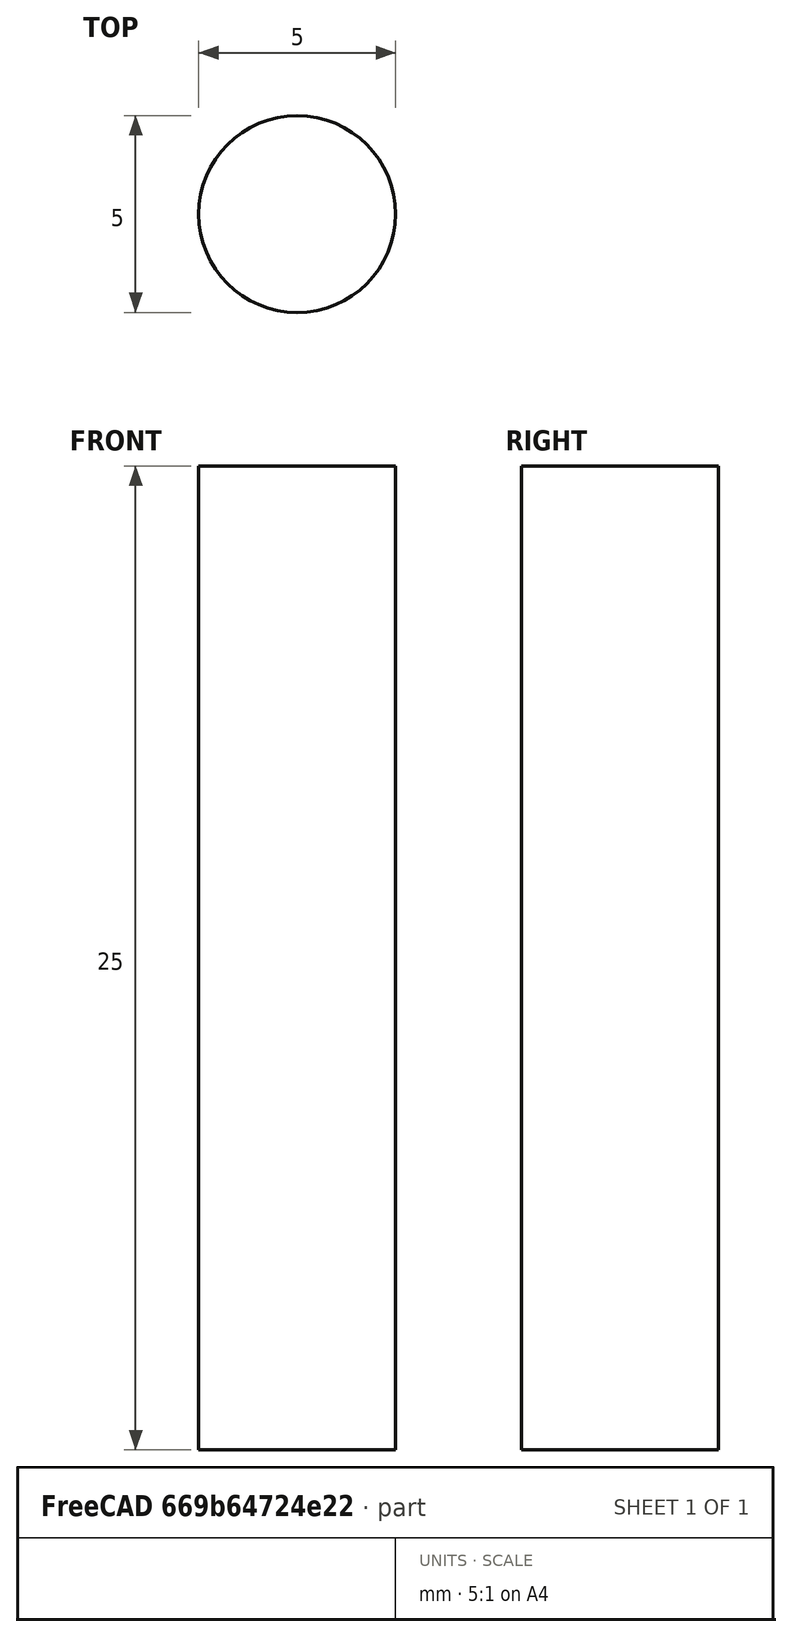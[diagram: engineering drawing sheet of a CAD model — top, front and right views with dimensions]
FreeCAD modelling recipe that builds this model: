
FCSTD DOCUMENT  (FreeCAD 1.0R39319 (Git))
Label: Airpods_2
License: All rights reserved
LicenseURL: https://en.wikipedia.org/wiki/All_rights_reserved
objects: Sketcher::SketchObject×6, Part::FeaturePython×5, Part::Part2DObjectPython×2, Part::Loft×2, Part::Extrusion×2, Part::MultiFuse×2, Part::RuledSurface×2, Part::Revolution×1, PartDesign::SubShapeBinder×1, App::DocumentObjectGroup×1
note: 29 computed .brp shape members not serialized (recipe doc carries the construction recipe); baked Part::Feature solids carry a one-line shape summary decoded from their .brp

FEATURE [Sketcher::SketchObject] Sketch  label="Front_profile"
  ArcFitTolerance = 1e-06
  FullyConstrained = true
  MakeInternals = false
  Placement = pos=(0,0,0) rot=(1,0,0;1.5708rad)
  sketch-geometry (18):
    g0-g4: Circle [constr] x5 (B-spline internal-alignment scaffolding for g5; pole/knot coordinates omitted)
    g5: BSplineCurve PolesCount=5 KnotsCount=3 Degree=3 IsPeriodic=0
    g6: GeomPoint [constr] X=-2 Y=0 Z=0
    g7: GeomPoint [constr] X=0 Y=3.5 Z=0
    g8: GeomPoint [constr] X=2 Y=0 Z=0
    g9: BSplineCurve PolesCount=5 KnotsCount=3 Degree=3 IsPeriodic=0
    g10-g14: Circle [constr] x5 (B-spline internal-alignment scaffolding for g9; pole/knot coordinates omitted)
    g15: GeomPoint [constr] X=-2 Y=0 Z=0
    g16: GeomPoint [constr] X=0 Y=-3.5 Z=0
    g17: GeomPoint [constr] X=2 Y=0 Z=0
  constraints (21):
    c: Weight(g0) = 1
    c: Equal(g0, g1-g4) x4
    c: InternalAlignment(g0-g4 -> g5) x5
    c: InternalAlignment(g6,g5)
    c: InternalAlignment(g7,g5)
    c: InternalAlignment(g8,g5)
    c: Distance(g0,g1) = 3.5
    c: PointOnObject(g0,g-1)
    c: PointOnObject(g2,g-2)
    c: PointOnObject(g4,g-1)
    c: Horizontal(g1,g3)
    c: Coincident(g7,g2)
    c: Vertical(g3,g5)
    c: Vertical(g1,g5)
    c: DistanceX(g5,g5) = 4
    c: Weight(g10) = 1
    c: Equal(g10, g11-g14) x4
    c: InternalAlignment(g10-g17 -> g9) x8
    c: Distance(g10,g11) = 3.5
    c: Coincident(g16,g12)
    c: Block(g9)
FEATURE [Sketcher::SketchObject] Sketch001  label="mid_profile"
  ArcFitTolerance = 1e-06
  FullyConstrained = true
  MakeInternals = false
  Placement = pos=(0,8,0) rot=(1,0,0;1.5708rad)
  sketch-geometry (5):
    g0: Ellipse CenterX=0 CenterY=0 CenterZ=0 NormalX=0 NormalY=0 NormalZ=1 MajorRadius=10 MinorRadius=6 AngleXU=-1.5708
    g1: LineSegment [constr] StartX=-3.26795e-06 StartY=-10 StartZ=0 EndX=3.26795e-06 EndY=10 EndZ=0
    g2: LineSegment [constr] StartX=6 StartY=-1.96077e-06 StartZ=0 EndX=-6 EndY=1.96077e-06 EndZ=0
    g3: GeomPoint [constr] X=-2.61436e-06 Y=-8 Z=0
    g4: GeomPoint [constr] X=2.61436e-06 Y=8 Z=0
  constraints (5):
    c: InternalAlignment(g1-g4 -> g0) x4
    c: Distance(g0,g1) = 10
    c: Angle(g1) = 1.5708
    c: Distance(g0,g2) = 6
    c: Coincident(g0,g-1)
FEATURE [Part::Part2DObjectPython] Clone2D  label="End_profile"  # Draft 2D object (typed FeaturePython)
  Fuse = false
  Objects = -> [Sketch001]
  Placement = pos=(0,10,0) rot=(1,0,0;1.5708rad)
  Scale = (1,1,1)
FEATURE [Part::Loft] Loft
  Closed = false
  MaxDegree = 5
  Ruled = false
  Sections = -> [Sketch,Sketch001,Clone2D]
  Solid = false
FEATURE [Sketcher::SketchObject] Sketch002  label="end_profilehalf"
  ArcFitTolerance = 1e-06
  ExternalGeometry = -> [Loft]
  FullyConstrained = true
  MakeInternals = false
  Placement = pos=(0,10,0) rot=(1,0,0;1.5708rad)
  sketch-geometry (5):
    g0: ArcOfEllipse CenterX=0 CenterY=0 CenterZ=0 NormalX=0 NormalY=0 NormalZ=1 MajorRadius=10 MinorRadius=6 AngleXU=-1.5708 StartAngle=1.5708 EndAngle=4.71239
    g1: LineSegment [constr] StartX=0 StartY=-10 StartZ=0 EndX=0 EndY=10 EndZ=0
    g2: LineSegment [constr] StartX=6 StartY=-1e-16 StartZ=0 EndX=-6 EndY=1e-16 EndZ=0
    g3: GeomPoint [constr] X=0 Y=-8 Z=0
    g4: GeomPoint [constr] X=0 Y=8 Z=0
  constraints (6):
    c: InternalAlignment(g1-g4 -> g0) x4
    c: Coincident(g0,g-1)
    c: Coincident(g0,g-3)
    c: PointOnObject(g0,g2)
    c: DistanceY(g-1,g1) = 10
    c: Vertical(g1)
FEATURE [Sketcher::SketchObject] Sketch003  label="Rev_axis_endproflie"
  ArcFitTolerance = 1e-06
  ExternalGeometry = -> [Loft]
  FullyConstrained = true
  MakeInternals = false
  sketch-geometry (1):
    g0: LineSegment StartX=-6 StartY=10 StartZ=0 EndX=6 EndY=10 EndZ=0
  constraints (2):
    c: Coincident(g0,g-3)
    c: Coincident(g0,g-4)
FEATURE [Part::Revolution] Revolve
  Angle = -180
  Axis = (1,0,0)
  AxisLink = -> Sketch003 [Edge1]
  Base = (6,10,0)
  FaceMakerClass = Part::FaceMakerBullseye
  Solid = false
  Source = -> Sketch002
  Symmetric = false
FEATURE [Sketcher::SketchObject] Sketch004
  ArcFitTolerance = 1e-06
  FullyConstrained = false
  MakeInternals = false
  sketch-geometry (9):
    g0-g4: Circle [constr] x5 (B-spline internal-alignment scaffolding for g5; pole/knot coordinates omitted)
    g5: BSplineCurve PolesCount=5 KnotsCount=3 Degree=3 IsPeriodic=0
    g6: GeomPoint [constr] X=-5.70514 Y=20.576 Z=0
    g7: GeomPoint [constr] X=-2.13381 Y=8.65962 Z=0
    g8: GeomPoint [constr] X=-5.35982 Y=-3.17422 Z=0
  constraints (6):
    c: Weight(g0) = 1
    c: Equal(g0, g1-g4) x4
    c: InternalAlignment(g0-g4 -> g5) x5
    c: InternalAlignment(g6,g5)
    c: InternalAlignment(g7,g5)
    c: InternalAlignment(g8,g5)
FEATURE [Part::Extrusion] Extrude
  Base = -> Sketch004
  Dir = (0,0,1)
  DirMode = 2
  FaceMakerClass = Part::FaceMakerBullseye
  FaceMakerMode = 3
  LengthFwd = 20
  LengthRev = 0
  Solid = false
  Symmetric = true
FEATURE [Part::MultiFuse] Fusion
  Refine = true
  Shapes = -> [Loft,Revolve]
FEATURE [Part::FeaturePython] Slice  # WARN: FeaturePython — macro-defined, semantics opaque (R4)
  Base = -> Fusion
  Mode = 1
  Tolerance = 0
  Tools = -> [Extrude]
FEATURE [Part::FeaturePython] Slice_child0  label="Slice.0"  # WARN: FeaturePython — macro-defined, semantics opaque (R4)
  Base = -> Slice
  FilterType = 1
  Invert = false
  OverrideMaxVal = 0
  WindowFrom = 80
  WindowTo = 100
  items = 0
FEATURE [Part::FeaturePython] Slice_child1  label="Slice.1"  # WARN: FeaturePython — macro-defined, semantics opaque (R4)
  Base = -> Slice
  FilterType = 1
  Invert = false
  OverrideMaxVal = 0
  WindowFrom = 80
  WindowTo = 100
  items = 1
FEATURE [Part::FeaturePython] Slice_child2  label="Slice.2"  # WARN: FeaturePython — macro-defined, semantics opaque (R4)
  Base = -> Slice
  FilterType = 1
  Invert = false
  OverrideMaxVal = 0
  WindowFrom = 80
  WindowTo = 100
  items = 2
FEATURE [Part::FeaturePython] Slice_child3  label="Slice.3"  # WARN: FeaturePython — macro-defined, semantics opaque (R4)
  Base = -> Slice
  FilterType = 1
  Invert = false
  OverrideMaxVal = 0
  WindowFrom = 80
  WindowTo = 100
  items = 3
FEATURE [Sketcher::SketchObject] Sketch005  label="Stem_profile"
  ArcFitTolerance = 1e-06
  FullyConstrained = true
  MakeInternals = false
  Placement = pos=(0,0,-5) rot=(0,0,1;0rad)
  sketch-geometry (1):
    g0: Circle CenterX=-10 CenterY=12 CenterZ=0 NormalX=0 NormalY=0 NormalZ=1 AngleXU=0 Radius=2.5
  constraints (3):
    c: Diameter(g0) = 5
    c: DistanceX(g0,g-1) = 10
    c: DistanceY(g-1,g0) = 12
FEATURE [Part::Extrusion] Extrude001
  Base = -> Sketch005
  Dir = (0,0,1)
  DirMode = 2
  FaceMakerClass = Part::FaceMakerBullseye
  FaceMakerMode = 3
  LengthFwd = -25
  LengthRev = 0
  Solid = true
  Symmetric = false
FEATURE [Part::Part2DObjectPython] Clone2D001  label="Stem_profile (2D)"  # Draft 2D object (typed FeaturePython)
  Fuse = false
  Objects = -> [Sketch005]
  Placement = pos=(-0.5,0,-5.86603) rot=(0,1,0;0.523599rad)
  Scale = (1,1,1)
FEATURE [PartDesign::SubShapeBinder] Binder
  BindCopyOnChange = 0
  BindMode = 0
  ClaimChildren = false
  Fuse = false
  MakeFace = true
  OffsetFill = false
  OffsetIntersection = false
  OffsetJoinType = 0
  OffsetOpenResult = false
  PartialLoad = false
  Refine = true
  Relative = true
  Support = -> [Slice_child2[Edge2],Slice_child0[Edge2,Edge10]]
  _Version = 2
FEATURE [Part::Loft] Loft001
  Closed = false
  MaxDegree = 5
  Ruled = false
  Sections = -> [Sketch005,Clone2D001,Binder]
  Solid = false
FEATURE [Part::RuledSurface] Ruled_Surface
  Curve1 = -> Slice_child0 [Edge6]
  Curve2 = -> Slice_child0 [Edge5]
  Orientation = 0
FEATURE [Part::RuledSurface] Ruled_Surface001
  Curve1 = -> Ruled_Surface [Edge2]
  Curve2 = -> Slice_child0 [Edge11]
  Orientation = 0
FEATURE [Part::MultiFuse] Fusion001
  Refine = true
  Shapes = -> [Loft001,Slice_child0,Ruled_Surface,Ruled_Surface001,Slice_child2]
FEATURE [App::DocumentObjectGroup] GrExplode_Slice  label="Exploded Slice"
  Group = -> [Slice_child1,Slice_child3,Fusion001]
